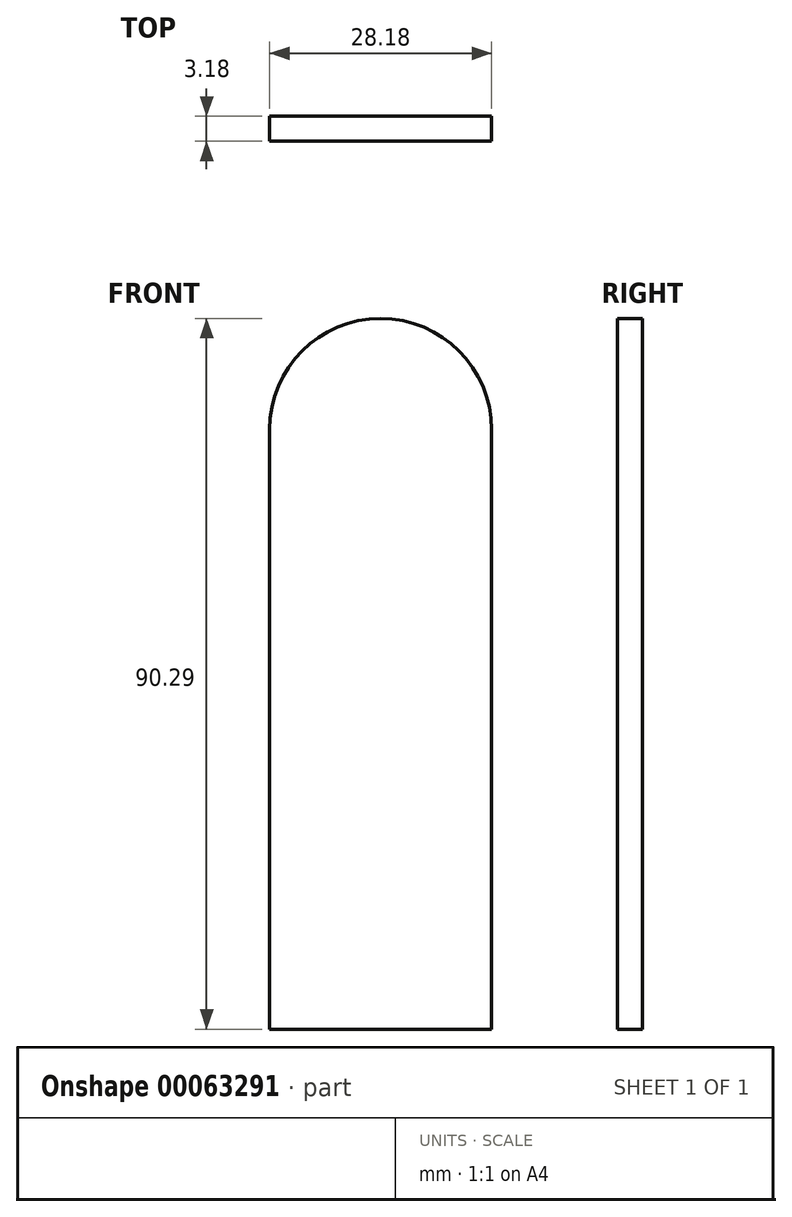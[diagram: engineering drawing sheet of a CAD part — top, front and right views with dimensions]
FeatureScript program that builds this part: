
annotation { "Feature Type Name" : "Feature", "Feature Type Description" : "" }
export const myFeature = defineFeature(function(context is Context, id is Id, definition is map)
    precondition{}
    {
        {
            var Q0;
            Q0=qCreatedBy(makeId("Front.planeOp"),FACE);
            var sketch = newSketch(context, id + "F0", { "sketchPlane" : qUnion([Q0])});
            skLineSegment(sketch, "E0.rect.top", {"start": v(14.1, -38.1) * mm, "end": v(-14.1, -38.1) * mm});
            skLineSegment(sketch, "E0.rect.left", {"start": v(14.1, 38.1) * mm, "end": v(14.1, -38.1) * mm});
            skLineSegment(sketch, "E0.rect.right", {"start": v(-14.1, 38.1) * mm, "end": v(-14.1, -38.1) * mm});
            skPoint(sketch, "E0.rect.middle", {"position": v(0, 0) * mm});
            skArc(sketch, "E1", {"start": v(14.1, 38.1) * mm, "mid": v(0, 52.2) * mm, "end": v(-14.1, 38.1) * mm});
            skSolve(sketch);
        }
        {
            var Q0;
            Q0 = qSketchRegion(id + "F0", true);
            extrude(context, id + "F1", {"entities" : qUnion([Q0]), "depth" : 3.17 * mm, "symmetric" : true});
        }
    });
